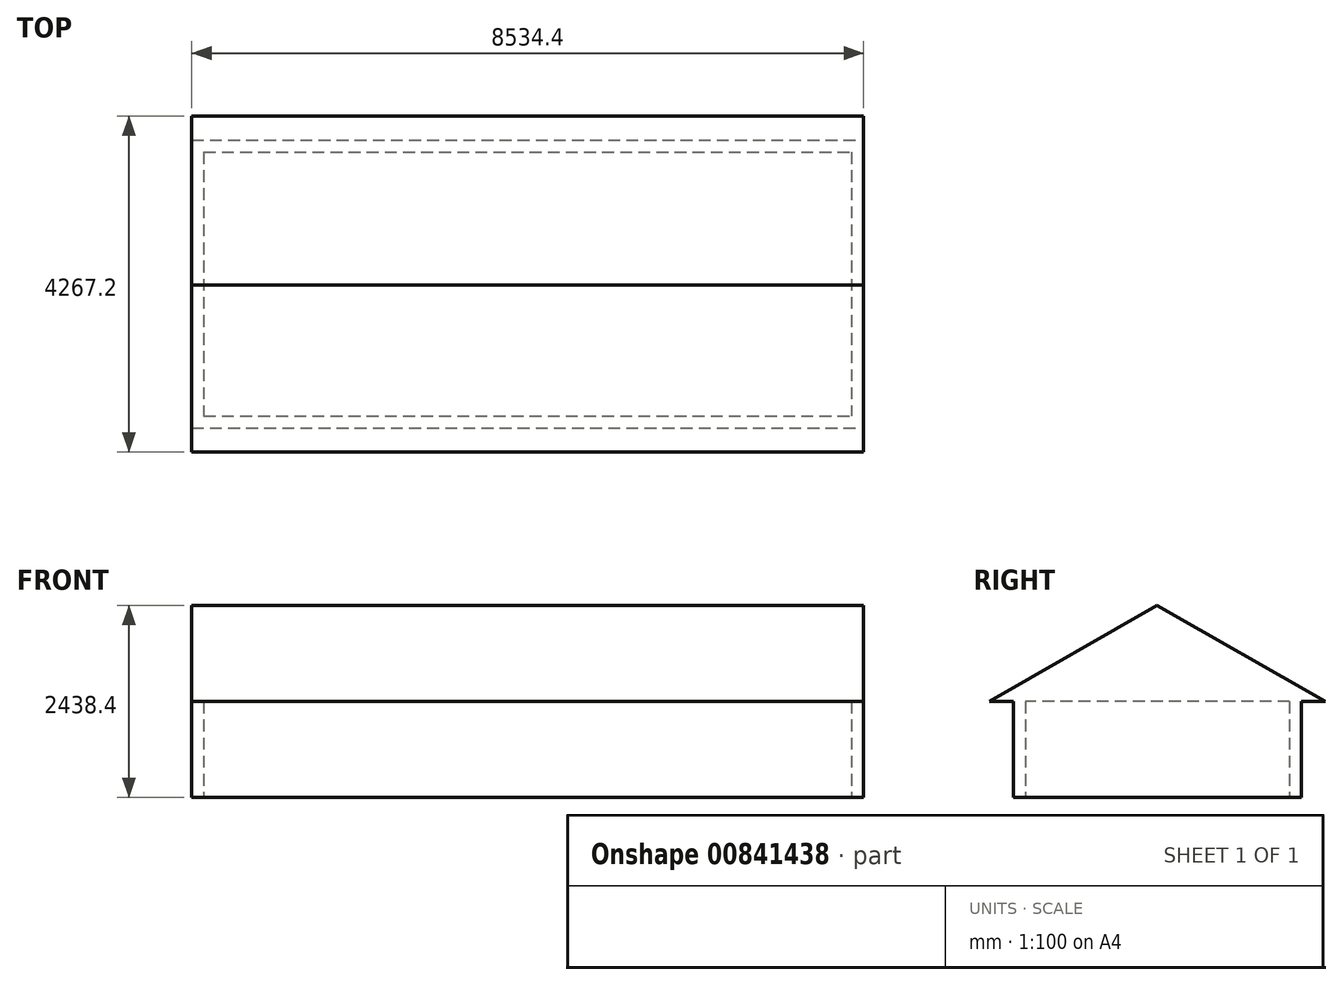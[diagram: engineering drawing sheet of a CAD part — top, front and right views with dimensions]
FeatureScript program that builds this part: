
annotation { "Feature Type Name" : "Feature", "Feature Type Description" : "" }
export const myFeature = defineFeature(function(context is Context, id is Id, definition is map)
    precondition{}
    {
        {
            var Q0;
            Q0=qCreatedBy(makeId("Top.planeOp"),FACE);
            var sketch = newSketch(context, id + "F0", { "sketchPlane" : qUnion([Q0])});
            skLineSegment(sketch, "E0.bottom", {"start": v(-7304.9, 1839.28) * mm, "end": v(1229.5, 1839.28) * mm});
            skLineSegment(sketch, "E0.top", {"start": v(-7304.9, -1818.32) * mm, "end": v(1229.5, -1818.32) * mm});
            skLineSegment(sketch, "E0.left", {"start": v(-7304.9, 1839.28) * mm, "end": v(-7304.9, -1818.32) * mm});
            skLineSegment(sketch, "E0.right", {"start": v(1229.5, 1839.28) * mm, "end": v(1229.5, -1818.32) * mm});
            skLineSegment(sketch, "E1.bottom", {"start": v(-7152.5, 1686.88) * mm, "end": v(1077.1, 1686.88) * mm});
            skLineSegment(sketch, "E1.top", {"start": v(-7152.5, -1665.92) * mm, "end": v(1077.1, -1665.92) * mm});
            skLineSegment(sketch, "E1.left", {"start": v(-7152.5, 1686.88) * mm, "end": v(-7152.5, -1665.92) * mm});
            skLineSegment(sketch, "E1.right", {"start": v(1077.1, 1686.88) * mm, "end": v(1077.1, -1665.92) * mm});
            skSolve(sketch);
        }
        {
            var Q0;
            Q0=makeQuery(id+"F0.imprint","IMPRINT",FACE,{"disambiguationData":[TD([[makeQuery(id+"F0.imprint","IMPRINT",EDGE,{"derivedFrom":sQuery(id+"F0.wireOp",EDGE,"E0.bottom")}),-1.0]])]});
            extrude(context, id + "F1", {"entities" : qUnion([Q0]), "depth" : 1219.2 * mm, "offsetDistance" : 30.48 * mm});
        }
        {
            var Q0;
            Q0=makeQuery(id+"F1.opExtrude","SWEPT_FACE",FACE,{"disambiguationData":[OSD([sQuery(id+"F0.wireOp",EDGE,"E0.right")])]});
            var sketch = newSketch(context, id + "F2", { "sketchPlane" : qUnion([Q0])});
            skLineSegment(sketch, "E2", {"start": v(-1818.32, 1219.2) * mm, "end": v(-2123.12, 1219.2) * mm});
            skLineSegment(sketch, "E3", {"start": v(-2123.12, 1219.2) * mm, "end": v(0, 2438.4) * mm});
            skLineSegment(sketch, "E4", {"start": v(0, 2438.4) * mm, "end": v(2144.08, 1219.2) * mm});
            skLineSegment(sketch, "E5", {"start": v(2144.08, 1219.2) * mm, "end": v(1839.28, 1219.2) * mm});
            skSolve(sketch);
        }
        {
            var Q0;
            Q0 = qSketchRegion(id + "F2", true);
            var Q1;
            Q1=makeQuery(id+"F2.imprint","IMPRINT",FACE,{"disambiguationData":[TD([[makeQuery(id+"F2.imprint","IMPRINT",EDGE,{"derivedFrom":sQuery(id+"F2.wireOp",EDGE,"E2")}),-1.0]])]});
            extrude(context, id + "F3", {"entities" : qUnion([Q0, Q1]), "operationType" : NewBodyOperationType.ADD, "oppositeDirection" : true, "depth" : 8534.4 * mm, "offsetDistance" : 30.48 * mm});
        }
    });
